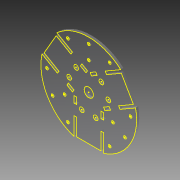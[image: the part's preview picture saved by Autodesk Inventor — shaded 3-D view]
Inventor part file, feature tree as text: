
AUTODESK INVENTOR PART (.ipt)
format: ipt  version: 2015 (Build 190159000, 159)  size: 312,832 bytes
history: native  units: mm
features: sketch x8, extrude x6, projected_geometry x4, pattern_circular x2
ambient origin geometry x8: Origin, YZ Plane, XZ Plane, XY Plane, X Axis, Y Axis, Z Axis, Center Point
bodies: Solid1 (feature_tree)
feature tree (20):
  extrude  "Extrusion1"  Depth=3.0mm TaperAngle=0.0deg
  extrude  "Extrusion2"  Depth=7.0mm
  extrude  "Extrusion3"  Depth=11.724mm
  extrude  "Extrusion4"  Depth=3.0mm
  extrude  "Extrusion5"  Depth=3.0mm TaperAngle=0.0deg
  pattern_circular  "Circular Pattern1"  [2 undecoded]
  sketch  "Sketch6"  dims[d12=5.0mm]
  pattern_circular  "Circular Pattern2"  [2 undecoded]
  extrude  "Extrusion6"  Depth=3.0mm TaperAngle=0.0deg
  sketch  "Sketch8"  dims[d14=20.006mm d15=5.0mm d16=3.0mm d17=0.0mm d18=3.0mm d19=0.0mm d20=48.0mm d21=10.0mm d22=3.0mm d23=0.0mm d24=30.0mm d25=360.0deg d27=30.0mm d28=360.0deg d30=60.0mm d31=90.0mm d32=30.0deg d33=30.0deg d34=30.0deg d35=30.0deg d36=30.0deg d37=30.0deg d38=120.0deg d39=120.0deg d40=3.0mm d41=3.0mm d42=3.0mm d43=3.0mm d44=3.0mm d45=3.0mm d46=3.0mm d47=3.0mm d48=3.0mm d49=3.0mm d50=3.0mm d51=3.0mm d52=3.0mm d53=0.0mm]
  sketch  "Sketch1"  dims[d0=103.0mm d1=3.0mm d2=0.0mm]
  sketch  "Sketch2"  dims[d3=10.906mm d4=7.0mm]
  projected_geometry  "Projected Loop1"
  sketch  "Sketch3"  dims[d5=11.724mm d6=40.0mm]
  sketch  "Sketch4"  dims[d7=32.0mm d8=3.0mm]
  projected_geometry  "Projected Loop2"
  sketch  "Sketch5"  dims[d9=3.0mm d10=3.0mm d11=0.0mm]
  sketch  "Sketch7"  dims[d13=15.0mm]
  projected_geometry  "Projected Loop3"
  projected_geometry  "Projected Loop4"
note: 4 required parameter values undecoded (feature->parameter linkage not recoverable at this tier; creation-order binding heuristic only, values carry confidence <= 0.55)
